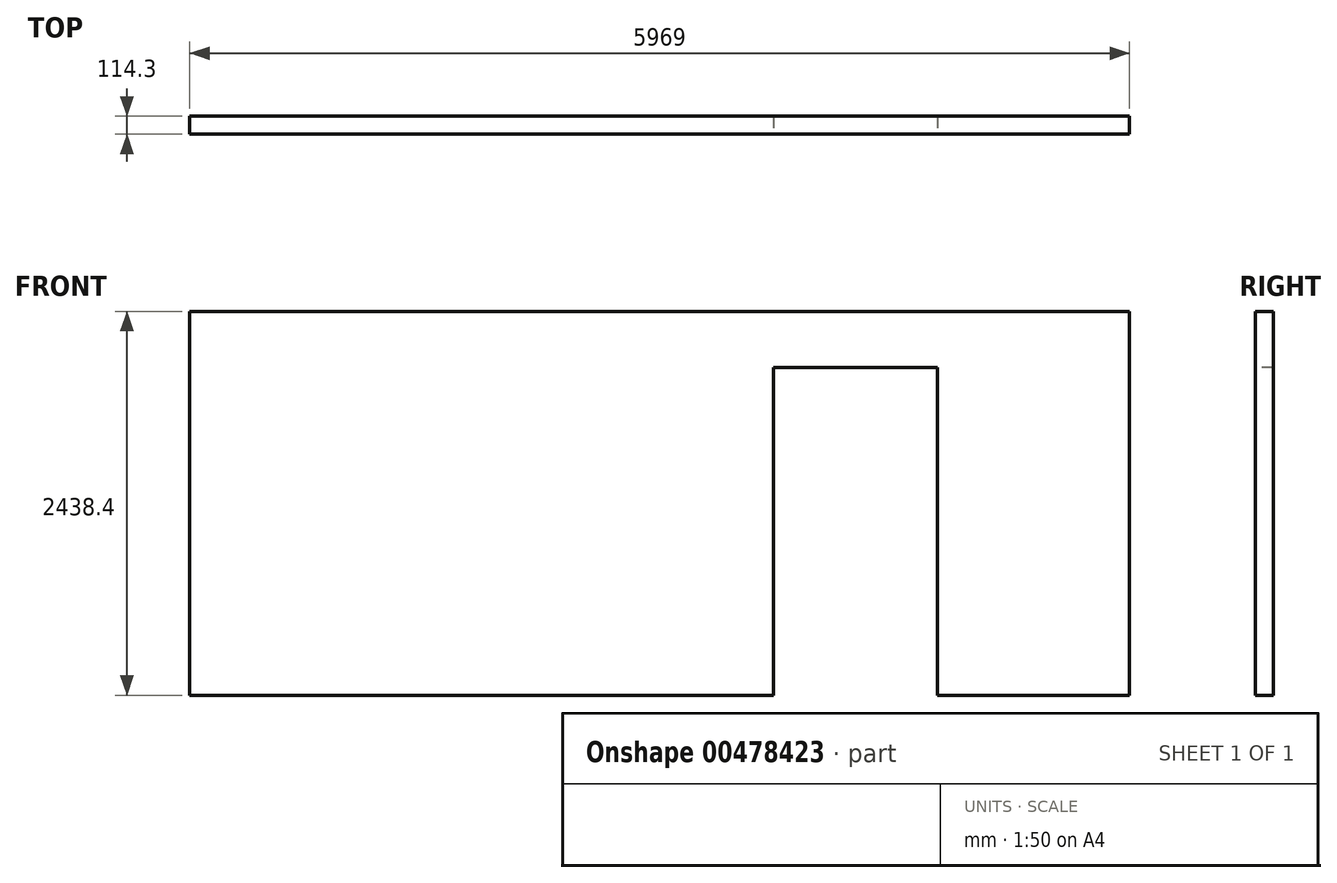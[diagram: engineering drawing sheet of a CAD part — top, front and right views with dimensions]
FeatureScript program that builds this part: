
annotation { "Feature Type Name" : "Feature", "Feature Type Description" : "" }
export const myFeature = defineFeature(function(context is Context, id is Id, definition is map)
    precondition{}
    {
        {
            var Q0;
            Q0=qCreatedBy(makeId("Top.planeOp"),FACE);
            var sketch = newSketch(context, id + "F0", { "sketchPlane" : qUnion([Q0])});
            skLineSegment(sketch, "E0.bottom", {"start": v(-2984.5, 57.15) * mm, "end": v(2984.5, 57.15) * mm});
            skLineSegment(sketch, "E0.top", {"start": v(-2984.5, -57.15) * mm, "end": v(2984.5, -57.15) * mm});
            skLineSegment(sketch, "E0.left", {"start": v(-2984.5, 57.15) * mm, "end": v(-2984.5, -57.15) * mm});
            skLineSegment(sketch, "E0.right", {"start": v(2984.5, 57.15) * mm, "end": v(2984.5, -57.15) * mm});
            skPoint(sketch, "E0.middle", {"position": v(0, 0) * mm});
            skSolve(sketch);
        }
        {
            var Q0;
            Q0 = qSketchRegion(id + "F0", true);
            extrude(context, id + "F1", {"entities" : qUnion([Q0]), "depth" : 2438.4 * mm});
        }
        {
            var Q0;
            Q0=makeQuery(id+"F1.opExtrude","SWEPT_FACE",FACE,{"disambiguationData":[OSD([sQuery(id+"F0.wireOp",EDGE,"E0.top")])]});
            var sketch = newSketch(context, id + "F2", { "sketchPlane" : qUnion([Q0])});
            skLineSegment(sketch, "E1", {"start": v(1765.3, 0) * mm, "end": v(1765.3, 2082.8) * mm});
            skLineSegment(sketch, "E2", {"start": v(1765.3, 2082.8) * mm, "end": v(723.9, 2082.8) * mm});
            skLineSegment(sketch, "E3", {"start": v(723.9, 2082.8) * mm, "end": v(723.9, 0) * mm});
            skLineSegment(sketch, "E4", {"start": v(1765.3, 0) * mm, "end": v(723.9, 0) * mm});
            skSolve(sketch);
        }
        {
            var Q0;
            Q0=makeQuery(id+"F2.imprint","IMPRINT",FACE,{"disambiguationData":[TD([[makeQuery(id+"F2.imprint","IMPRINT",EDGE,{"derivedFrom":sQuery(id+"F2.wireOp",EDGE,"E1")}),1.0]])]});
            extrude(context, id + "F3", {"entities" : qUnion([Q0]), "operationType" : NewBodyOperationType.REMOVE, "oppositeDirection" : true, "depth" : 114.3 * mm});
        }
    });
